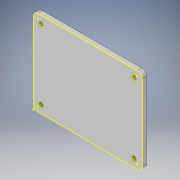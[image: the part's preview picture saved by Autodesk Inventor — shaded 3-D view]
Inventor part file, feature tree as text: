
AUTODESK INVENTOR PART (.ipt)
format: ipt  version: 2019 (Build 230136000, 136)  size: 121,344 bytes
history: native  units: mm
features: sketch x3, extrude x1, hole x1, fillet x1, projected_geometry x1
ambient origin geometry x8: Origin, YZ Plane, XZ Plane, XY Plane, X Axis, Y Axis, Z Axis, Center Point
bodies: Solid1 (feature_tree)
feature tree (7):
  sketch  "Sketch1"  dims[d0=70.0mm d1=55.0mm]
  extrude  "Extrusion1"  Depth=55.0mm
  hole  "Hole1"  [1 undecoded]
  fillet  "Fillet1"  Radius=60.0mm
  sketch  "Sketch4"  dims[d19=45.0mm d20=70.0mm d21=55.0mm d22=5.0mm d23=5.0mm d24=60.0mm d25=45.0mm d26=3.0mm d27=0.0mm d28=3.3mm d29=6.0mm d30=4.0mm d31=2.0mm d32=90.0deg d33=8.0mm d34=20.594885mm d35=3.0mm]
  sketch  "Sketch3"  dims[d13=5.0mm d14=5.0mm d18=60.0mm]
  projected_geometry  "Projected Loop1"
note: 1 required parameter value undecoded (feature->parameter linkage not recoverable at this tier; creation-order binding heuristic only, values carry confidence <= 0.55)
